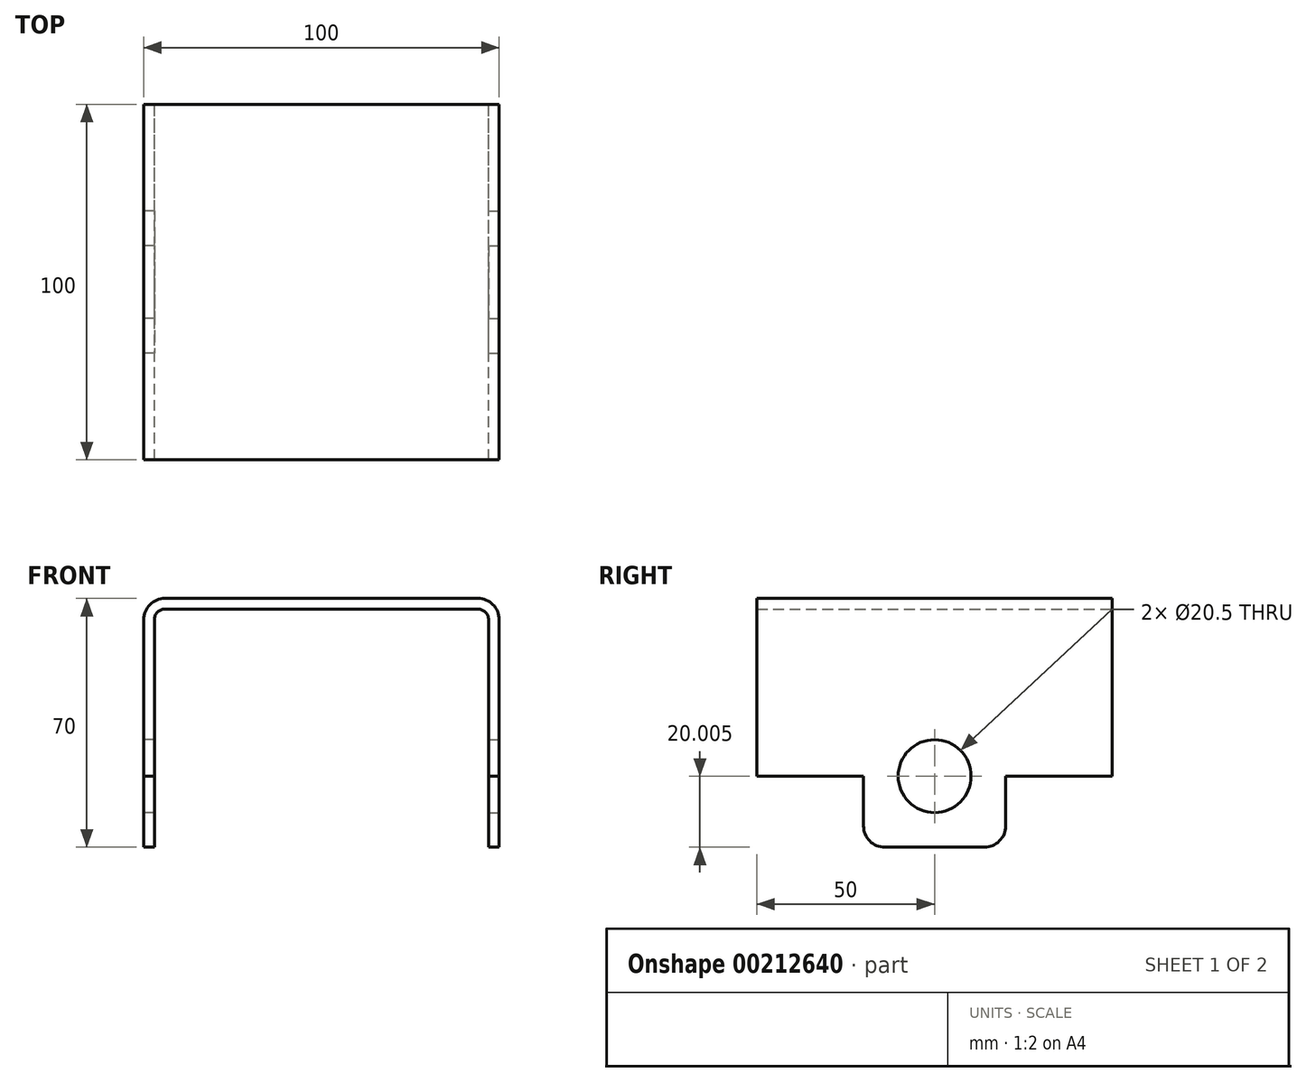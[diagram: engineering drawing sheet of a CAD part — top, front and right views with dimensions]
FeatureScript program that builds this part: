
annotation { "Feature Type Name" : "Feature", "Feature Type Description" : "" }
export const myFeature = defineFeature(function(context is Context, id is Id, definition is map)
    precondition{}
    {
        {
            var Q0;
            Q0=qCreatedBy(makeId("Front.planeOp"),FACE);
            var sketch = newSketch(context, id + "F0", { "sketchPlane" : qUnion([Q0])});
            skLineSegment(sketch, "E0", {"start": v(0, 20.85) * mm, "end": v(44, 20.85) * mm});
            skLineSegment(sketch, "E1", {"start": v(47, 17.85) * mm, "end": v(47, -26.15) * mm});
            skLineSegment(sketch, "E2", {"start": v(47, -26.15) * mm, "end": v(50, -26.15) * mm});
            skLineSegment(sketch, "E3", {"start": v(50, -26.15) * mm, "end": v(50, 17.85) * mm});
            skLineSegment(sketch, "E4", {"start": v(44, 23.85) * mm, "end": v(0, 23.85) * mm});
            skLineSegment(sketch, "E5", {"start": v(0, 20.85) * mm, "end": v(0, 23.85) * mm});
            skArc(sketch, "E6.filletArc", {"start": v(47, 17.85) * mm, "mid": v(46.12, 19.98) * mm, "end": v(44, 20.85) * mm});
            skArc(sketch, "E7.filletArc", {"start": v(50, 17.85) * mm, "mid": v(48.24, 22.1) * mm, "end": v(44, 23.85) * mm});
            skLineSegment(sketch, "E8.MirrorCS", {"start": v(-47, -26.15) * mm, "end": v(-50, -26.15) * mm});
            skArc(sketch, "E9.MirrorCS", {"start": v(-47, 17.85) * mm, "mid": v(-46.12, 19.98) * mm, "end": v(-44, 20.85) * mm});
            skLineSegment(sketch, "E10.MirrorCS", {"start": v(0, 20.85) * mm, "end": v(-44, 20.85) * mm});
            skLineSegment(sketch, "E11.MirrorCS", {"start": v(-47, 17.85) * mm, "end": v(-47, -26.15) * mm});
            skLineSegment(sketch, "E12.MirrorCS", {"start": v(-44, 23.85) * mm, "end": v(0, 23.85) * mm});
            skPoint(sketch, "E13.MirrorP", {"position": v(-47, 20.85) * mm});
            skPoint(sketch, "E14.MirrorP", {"position": v(-50, 23.85) * mm});
            skArc(sketch, "E15.MirrorCS", {"start": v(-50, 17.85) * mm, "mid": v(-48.24, 22.1) * mm, "end": v(-44, 23.85) * mm});
            skLineSegment(sketch, "E16.MirrorCS", {"start": v(-50, -26.15) * mm, "end": v(-50, 17.85) * mm});
            skSolve(sketch);
        }
        {
            var Q0;
            Q0=makeQuery(id+"F0.imprint","IMPRINT",FACE,{"disambiguationData":[TD([[makeQuery(id+"F0.imprint","IMPRINT",EDGE,{"derivedFrom":sQuery(id+"F0.wireOp",EDGE,"E5")}),1.0]])]});
            var Q1;
            Q1=makeQuery(id+"F0.imprint","IMPRINT",FACE,{"disambiguationData":[TD([[makeQuery(id+"F0.imprint","IMPRINT",EDGE,{"derivedFrom":sQuery(id+"F0.wireOp",EDGE,"E0")}),1.0]])]});
            var Q2;
            Q2=makeQuery(id+"F0.imprint","IMPRINT",FACE,{"disambiguationData":[TD([[makeQuery(id+"F0.imprint","IMPRINT",EDGE,{"derivedFrom":sQuery(id+"F0.wireOp",EDGE,"cd8f01d6-81fd-49a1-aa39-a206505facb41.MirrorCS")}),-1.0]])]});
            var Q3;
            Q3=makeQuery(id+"F0.imprint","IMPRINT",FACE,{"disambiguationData":[TD([[makeQuery(id+"F0.imprint","IMPRINT",EDGE,{"derivedFrom":sQuery(id+"F0.wireOp",EDGE,"E3")}),-1.0]])]});
            extrude(context, id + "F1", {"entities" : qUnion([Q0, Q1, Q2, Q3]), "depth" : 100 * mm});
        }
        {
            var Q0;
            Q0=makeQuery(id+"F1.opExtrude","SWEPT_FACE",FACE,{"disambiguationData":[OSD([sQuery(id+"F0.wireOp",EDGE,"E16.MirrorCS")])]});
            var sketch = newSketch(context, id + "F2", { "sketchPlane" : qUnion([Q0])});
            skLineSegment(sketch, "E17.bottom", {"start": v(30, -26.15) * mm, "end": v(70, -26.15) * mm});
            skLineSegment(sketch, "E17.top", {"start": v(36, -46.15) * mm, "end": v(64, -46.15) * mm});
            skLineSegment(sketch, "E17.left", {"start": v(30, -26.15) * mm, "end": v(30, -40.15) * mm});
            skLineSegment(sketch, "E17.right", {"start": v(70, -26.15) * mm, "end": v(70, -40.15) * mm});
            skCircle(sketch, "E18", {"center": v(50, -26.15) * mm, "radius": 10.25 * mm});
            skPoint(sketch, "E19.visualSharp", {"position": v(30, -46.15) * mm});
            skArc(sketch, "E19.filletArc", {"start": v(30, -40.15) * mm, "mid": v(31.76, -44.39) * mm, "end": v(36, -46.15) * mm});
            skPoint(sketch, "E20.visualSharp", {"position": v(70, -46.15) * mm});
            skArc(sketch, "E20.filletArc", {"start": v(64, -46.15) * mm, "mid": v(68.24, -44.39) * mm, "end": v(70, -40.15) * mm});
            skSolve(sketch);
        }
        {
            var Q0;
            {var subQ0=sQuery(id+"F2.wireOp",EDGE,"E18");var subQ1=sQuery(id+"F2.wireOp",EDGE,"E17.bottom");var subQ2=makeQuery(id+"F2.imprint","INTERSECT",VERTEX,{"disambiguationData":[OD(0.0)],"derivedFrom":[subQ1,subQ0]});Q0=makeQuery(id+"F2.imprint","IMPRINT",FACE,{"disambiguationData":[TD([[makeQuery(id+"F2.imprint","IMPRINT",EDGE,{"disambiguationData":[TD([[subQ2,-1.0]])],"derivedFrom":subQ1}),-1.0]])]});}
            var Q1;
            {var subQ0=sQuery(id+"F2.wireOp",EDGE,"E18");var subQ1=sQuery(id+"F2.wireOp",EDGE,"E17.bottom");var subQ2=makeQuery(id+"F2.imprint","INTERSECT",VERTEX,{"disambiguationData":[OD(0.0)],"derivedFrom":[subQ1,subQ0]});Q1=makeQuery(id+"F2.imprint","IMPRINT",FACE,{"disambiguationData":[TD([[makeQuery(id+"F2.imprint","IMPRINT",EDGE,{"disambiguationData":[TD([[subQ2,-1.0]])],"derivedFrom":subQ1}),-1.0]])]});}
            extrude(context, id + "F3", {"entities" : qUnion([Q0, Q1]), "operationType" : NewBodyOperationType.REMOVE, "oppositeDirection" : true, "depth" : 3 * mm});
        }
        {
            var Q0;
            Q0=makeQuery(id+"F2.imprint","IMPRINT",FACE,{"disambiguationData":[TD([[makeQuery(id+"F2.imprint","IMPRINT",EDGE,{"derivedFrom":sQuery(id+"F2.wireOp",EDGE,"E17.top")}),1.0]])]});
            var Q1;
            Q1=makeQuery(id+"F2.imprint","IMPRINT",FACE,{"disambiguationData":[TD([[makeQuery(id+"F2.imprint","IMPRINT",EDGE,{"derivedFrom":sQuery(id+"F2.wireOp",EDGE,"E17.top")}),1.0]])]});
            extrude(context, id + "F4", {"entities" : qUnion([Q0, Q1]), "operationType" : NewBodyOperationType.ADD, "oppositeDirection" : true, "depth" : 3 * mm});
        }
        {
            var Q0;
            Q0=makeQuery(id+"F1.opExtrude","SWEPT_FACE",FACE,{"disambiguationData":[OSD([sQuery(id+"F0.wireOp",EDGE,"E3")])]});
            var sketch = newSketch(context, id + "F5", { "sketchPlane" : qUnion([Q0])});
            skLineSegment(sketch, "E21.bottom", {"start": v(-70, -26.15) * mm, "end": v(-30, -26.15) * mm});
            skLineSegment(sketch, "E21.top", {"start": v(-64, -46.15) * mm, "end": v(-36, -46.15) * mm});
            skLineSegment(sketch, "E21.left", {"start": v(-70, -26.15) * mm, "end": v(-70, -40.15) * mm});
            skLineSegment(sketch, "E21.right", {"start": v(-30, -26.15) * mm, "end": v(-30, -40.15) * mm});
            skPoint(sketch, "E22.visualSharp", {"position": v(-70, -46.15) * mm});
            skArc(sketch, "E22.filletArc", {"start": v(-70, -40.15) * mm, "mid": v(-68.24, -44.39) * mm, "end": v(-64, -46.15) * mm});
            skPoint(sketch, "E23.visualSharp", {"position": v(-30, -46.15) * mm});
            skArc(sketch, "E23.filletArc", {"start": v(-36, -46.15) * mm, "mid": v(-31.76, -44.39) * mm, "end": v(-30, -40.15) * mm});
            skSolve(sketch);
        }
        {
            var Q0;
            Q0 = qSketchRegion(id + "F5", true);
            extrude(context, id + "F6", {"entities" : qUnion([Q0]), "operationType" : NewBodyOperationType.ADD, "oppositeDirection" : true, "depth" : 3 * mm});
        }
        {
            var Q0;
            Q0=makeQuery(id+"F6.boolean.opBoolean","MERGE",FACE,{"derivedFrom":[makeQuery(id+"F1.opExtrude","SWEPT_FACE",FACE,{"disambiguationData":[OSD([sQuery(id+"F0.wireOp",EDGE,"E3")])]}),makeQuery(id+"F6.opExtrude","CAP_FACE",FACE,{"disambiguationData":[OSD([sQuery(id+"F5.wireOp",EDGE,"E21.bottom"),sQuery(id+"F5.wireOp",EDGE,"E21.top"),sQuery(id+"F5.wireOp",EDGE,"E21.left"),sQuery(id+"F5.wireOp",EDGE,"E21.right"),sQuery(id+"F5.wireOp",EDGE,"E22.filletArc"),sQuery(id+"F5.wireOp",EDGE,"E23.filletArc")])],"isStart":true})]});
            var sketch = newSketch(context, id + "F7", { "sketchPlane" : qUnion([Q0])});
            skCircle(sketch, "E24", {"center": v(-50, -26.15) * mm, "radius": 10.25 * mm});
            skSolve(sketch);
        }
        {
            var Q0;
            Q0 = qSketchRegion(id + "F7", true);
            extrude(context, id + "F8", {"entities" : qUnion([Q0]), "operationType" : NewBodyOperationType.REMOVE, "oppositeDirection" : true, "depth" : 3 * mm});
        }
    });
